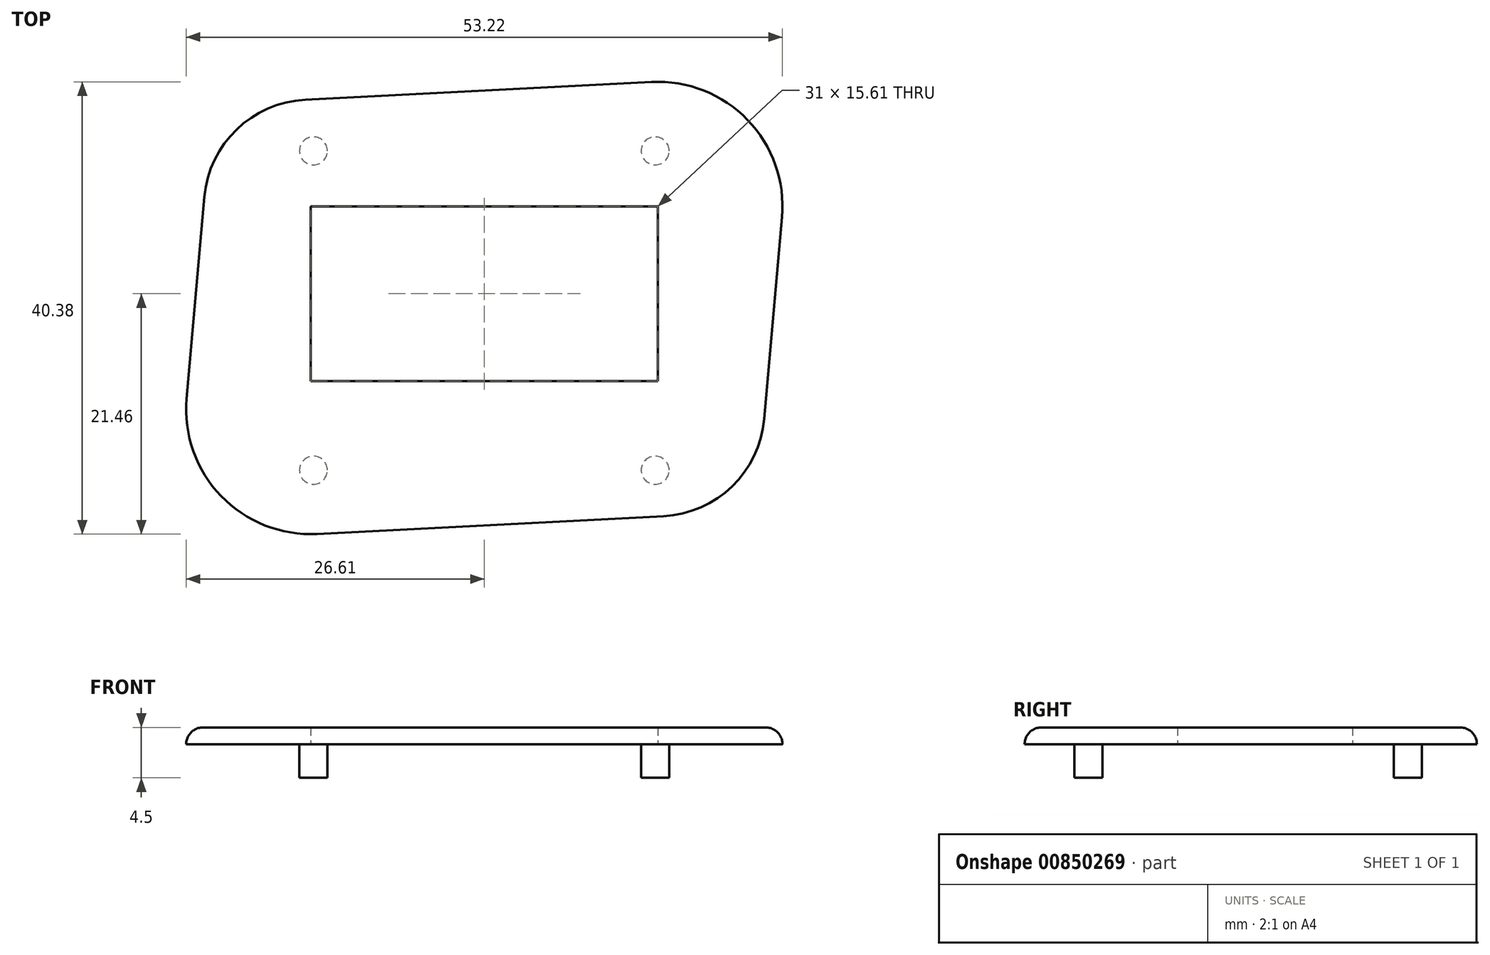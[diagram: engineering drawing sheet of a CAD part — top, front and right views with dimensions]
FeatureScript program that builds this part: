
annotation { "Feature Type Name" : "Feature", "Feature Type Description" : "" }
export const myFeature = defineFeature(function(context is Context, id is Id, definition is map)
    precondition{}
    {
        {
            var Q0;
            Q0=qCreatedBy(makeId("Top.planeOp"),FACE);
            var sketch = newSketch(context, id + "F0", { "sketchPlane" : qUnion([Q0])});
            skLineSegment(sketch, "E0.bottom", {"start": v(17.5, 16.75) * mm, "end": v(-17.5, 16.75) * mm});
            skLineSegment(sketch, "E0.top", {"start": v(17.5, -16.75) * mm, "end": v(-17.5, -16.75) * mm});
            skLineSegment(sketch, "E0.left", {"start": v(17.5, 16.75) * mm, "end": v(17.5, -16.75) * mm});
            skLineSegment(sketch, "E0.right", {"start": v(-17.5, 16.75) * mm, "end": v(-17.5, -16.75) * mm});
            skPoint(sketch, "E0.middle", {"position": v(0, 0) * mm});
            skLineSegment(sketch, "E1.bottom", {"start": v(17.5, 11.3) * mm, "end": v(-17.5, 11.3) * mm});
            skLineSegment(sketch, "E1.top", {"start": v(17.5, -11.3) * mm, "end": v(-17.5, -11.3) * mm});
            skLineSegment(sketch, "E1.left", {"start": v(17.5, 11.3) * mm, "end": v(17.5, -11.3) * mm});
            skLineSegment(sketch, "E1.right", {"start": v(-17.5, 11.3) * mm, "end": v(-17.5, -11.3) * mm});
            skCircle(sketch, "E2", {"center": v(-15.25, 14.25) * mm, "radius": 1.25 * mm});
            skLineSegment(sketch, "E3.bottom", {"start": v(15.25, 14.25) * mm, "end": v(-15.25, 14.25) * mm, "construction": true});
            skLineSegment(sketch, "E3.top", {"start": v(15.25, -14.25) * mm, "end": v(-15.25, -14.25) * mm, "construction": true});
            skLineSegment(sketch, "E3.left", {"start": v(15.25, 14.25) * mm, "end": v(15.25, -14.25) * mm, "construction": true});
            skLineSegment(sketch, "E3.right", {"start": v(-15.25, 14.25) * mm, "end": v(-15.25, -14.25) * mm, "construction": true});
            skCircle(sketch, "E4", {"center": v(15.25, 14.25) * mm, "radius": 1.25 * mm});
            skCircle(sketch, "E5", {"center": v(-15.25, -14.25) * mm, "radius": 1.25 * mm});
            skCircle(sketch, "E6", {"center": v(15.25, -14.25) * mm, "radius": 1.25 * mm});
            skLineSegment(sketch, "E7.bottom", {"start": v(-17.5, 16.75) * mm, "end": v(-19, 16.75) * mm});
            skLineSegment(sketch, "E7.top", {"start": v(-17.5, -16.75) * mm, "end": v(-19, -16.75) * mm});
            skLineSegment(sketch, "E7.right", {"start": v(-19, 16.75) * mm, "end": v(-19, -16.75) * mm});
            skLineSegment(sketch, "E8.bottom", {"start": v(17.5, -16.75) * mm, "end": v(19, -16.75) * mm});
            skLineSegment(sketch, "E8.top", {"start": v(17.5, 16.75) * mm, "end": v(19, 16.75) * mm});
            skLineSegment(sketch, "E8.left", {"start": v(17.5, -16.75) * mm, "end": v(17.5, 16.75) * mm});
            skLineSegment(sketch, "E8.right", {"start": v(19, -16.75) * mm, "end": v(19, 16.75) * mm});
            skSolve(sketch);
        }
        {
            var Q0;
            {var subQ3=sQuery(id+"F0.wireOp",EDGE,"E7.bottom");Q0=makeQuery(id+"F0.imprint","IMPRINT",FACE,{"disambiguationData":[TD([[makeQuery(id+"F0.imprint","IMPRINT",EDGE,{"derivedFrom":subQ3}),1.0]])]});}
            var Q1;
            {var subQ1=sQuery(id+"F0.wireOp",EDGE,"E0.bottom");Q1=makeQuery(id+"F0.imprint","IMPRINT",FACE,{"disambiguationData":[TD([[makeQuery(id+"F0.imprint","IMPRINT",EDGE,{"derivedFrom":subQ1}),1.0]])]});}
            var Q2;
            {var subQ3=sQuery(id+"F0.wireOp",EDGE,"E8.bottom");Q2=makeQuery(id+"F0.imprint","IMPRINT",FACE,{"disambiguationData":[TD([[makeQuery(id+"F0.imprint","IMPRINT",EDGE,{"derivedFrom":subQ3}),1.0]])]});}
            var Q3;
            {var subQ1=sQuery(id+"F0.wireOp",EDGE,"E0.top");Q3=makeQuery(id+"F0.imprint","IMPRINT",FACE,{"disambiguationData":[TD([[makeQuery(id+"F0.imprint","IMPRINT",EDGE,{"derivedFrom":subQ1}),-1.0]])]});}
            extrude(context, id + "F1", {"entities" : qUnion([Q0, Q1, Q2, Q3]), "depth" : 1.5 * mm, "offsetDistance" : 25.4 * mm});
        }
        {
            var Q0;
            Q0=qCreatedBy(makeId("Top.planeOp"),FACE);
            var sketch = newSketch(context, id + "F2", { "sketchPlane" : qUnion([Q0])});
            skLineSegment(sketch, "E9.bottom", {"start": v(-15.5, -6.3) * mm, "end": v(15.5, -6.3) * mm});
            skLineSegment(sketch, "E9.top", {"start": v(-15.5, 9.3) * mm, "end": v(15.5, 9.3) * mm});
            skLineSegment(sketch, "E9.left", {"start": v(-15.5, -6.3) * mm, "end": v(-15.5, 9.3) * mm});
            skLineSegment(sketch, "E9.right", {"start": v(15.5, -6.3) * mm, "end": v(15.5, 9.3) * mm});
            skLineSegment(sketch, "E10.0", {"start": v(-17.5, 11.3) * mm, "end": v(-17.5, -11.3) * mm});
            skLineSegment(sketch, "E10.1", {"start": v(17.5, 11.3) * mm, "end": v(-17.5, 11.3) * mm});
            skLineSegment(sketch, "E10.2", {"start": v(17.5, -11.3) * mm, "end": v(17.5, 11.3) * mm});
            skLineSegment(sketch, "E10.3", {"start": v(17.5, -11.3) * mm, "end": v(-17.5, -11.3) * mm});
            skSolve(sketch);
        }
        {
            var Q0;
            Q0=makeQuery(id+"F2.imprint","IMPRINT",FACE,{"disambiguationData":[TD([[makeQuery(id+"F2.imprint","IMPRINT",EDGE,{"derivedFrom":sQuery(id+"F2.wireOp",EDGE,"E9.bottom")}),-1.0]])]});
            var Q1;
            {var subQ0=sQuery(id+"F0.wireOp",EDGE,"E8.right");var subQ1=sQuery(id+"F0.wireOp",EDGE,"E8.top");var subQ2=sQuery(id+"F0.wireOp",EDGE,"E8.bottom");var subQ3=sQuery(id+"F0.wireOp",EDGE,"E7.right");var subQ4=sQuery(id+"F0.wireOp",EDGE,"E7.top");var subQ5=sQuery(id+"F0.wireOp",EDGE,"E7.bottom");var subQ6=sQuery(id+"F0.wireOp",EDGE,"E0.top");var subQ7=sQuery(id+"F0.wireOp",EDGE,"E0.bottom");Q1=makeQuery(id+"F8.boolean.opBoolean","MERGE",FACE,{"derivedFrom":[makeQuery(id+"F5.boolean.opBoolean","MERGE",FACE,{"derivedFrom":[makeQuery(id+"F1.opExtrude","CAP_FACE",FACE,{"disambiguationData":[OSD([subQ7,subQ6,sQuery(id+"F0.wireOp",EDGE,"E1.bottom"),sQuery(id+"F0.wireOp",EDGE,"E1.top"),sQuery(id+"F0.wireOp",EDGE,"E2"),sQuery(id+"F0.wireOp",EDGE,"E4"),sQuery(id+"F0.wireOp",EDGE,"E5"),sQuery(id+"F0.wireOp",EDGE,"E6"),subQ5,subQ4,sQuery(id+"F0.wireOp",EDGE,"E0.right"),subQ3,subQ2,subQ1,sQuery(id+"F0.wireOp",EDGE,"E8.left"),subQ0])],"isStart":false}),makeQuery(id+"F5.opExtrude","CAP_FACE",FACE,{"disambiguationData":[OSD([sQuery(id+"F4.wireOp",EDGE,"E11.0")])],"isStart":true}),makeQuery(id+"F5.opExtrude","CAP_FACE",FACE,{"disambiguationData":[OSD([sQuery(id+"F4.wireOp",EDGE,"E11.1")])],"isStart":true}),makeQuery(id+"F5.opExtrude","CAP_FACE",FACE,{"disambiguationData":[OSD([sQuery(id+"F4.wireOp",EDGE,"E11.2")])],"isStart":true}),makeQuery(id+"F5.opExtrude","CAP_FACE",FACE,{"disambiguationData":[OSD([sQuery(id+"F4.wireOp",EDGE,"E11.3")])],"isStart":true})]}),makeQuery(id+"F8.opExtrude","CAP_FACE",FACE,{"disambiguationData":[OSD([subQ7,subQ6,subQ5,subQ4,subQ3,subQ2,subQ1,subQ0,sQuery(id+"F6.wireOp",EDGE,"E12"),sQuery(id+"F6.wireOp",EDGE,"E13"),sQuery(id+"F6.wireOp",EDGE,"E14"),sQuery(id+"F6.wireOp",EDGE,"E15"),sQuery(id+"F6.wireOp",EDGE,"E16"),sQuery(id+"F6.wireOp",EDGE,"E17"),sQuery(id+"F6.wireOp",EDGE,"E18"),sQuery(id+"F6.wireOp",EDGE,"E19")])],"isStart":true})]});}
            extrude(context, id + "F3", {"entities" : qUnion([Q0]), "operationType" : NewBodyOperationType.ADD, "endBound" : BoundingType.UP_TO_SURFACE, "depth" : 25.4 * mm, "endBoundEntityFace" : qUnion([Q1]), "offsetDistance" : 25.4 * mm});
        }
        {
            var Q0;
            Q0=makeQuery(id+"F1.opExtrude","CAP_FACE",FACE,{"disambiguationData":[OSD([sQuery(id+"F0.wireOp",EDGE,"E0.bottom"),sQuery(id+"F0.wireOp",EDGE,"E0.top"),sQuery(id+"F0.wireOp",EDGE,"E1.bottom"),sQuery(id+"F0.wireOp",EDGE,"E1.top"),sQuery(id+"F0.wireOp",EDGE,"E2"),sQuery(id+"F0.wireOp",EDGE,"E4"),sQuery(id+"F0.wireOp",EDGE,"E5"),sQuery(id+"F0.wireOp",EDGE,"E6"),sQuery(id+"F0.wireOp",EDGE,"E7.bottom"),sQuery(id+"F0.wireOp",EDGE,"E7.top"),sQuery(id+"F0.wireOp",EDGE,"E0.right"),sQuery(id+"F0.wireOp",EDGE,"E7.right"),sQuery(id+"F0.wireOp",EDGE,"E8.bottom"),sQuery(id+"F0.wireOp",EDGE,"E8.top"),sQuery(id+"F0.wireOp",EDGE,"E8.left"),sQuery(id+"F0.wireOp",EDGE,"E8.right")])],"isStart":false});
            var sketch = newSketch(context, id + "F4", { "sketchPlane" : qUnion([Q0])});
            skCircle(sketch, "E11.0", {"center": v(-15.25, 14.25) * mm, "radius": 1.25 * mm});
            skCircle(sketch, "E11.1", {"center": v(15.25, 14.25) * mm, "radius": 1.25 * mm});
            skCircle(sketch, "E11.2", {"center": v(15.25, -14.25) * mm, "radius": 1.25 * mm});
            skCircle(sketch, "E11.3", {"center": v(-15.25, -14.25) * mm, "radius": 1.25 * mm});
            skSolve(sketch);
        }
        {
            var Q0;
            Q0 = qSketchRegion(id + "F4", true);
            extrude(context, id + "F5", {"entities" : qUnion([Q0]), "operationType" : NewBodyOperationType.ADD, "oppositeDirection" : true, "depth" : 4.5 * mm, "offsetDistance" : 25.4 * mm});
        }
        {
            var Q0;
            Q0=makeQuery(id+"F5.boolean.opBoolean","MERGE",FACE,{"derivedFrom":[makeQuery(id+"F1.opExtrude","CAP_FACE",FACE,{"disambiguationData":[OSD([sQuery(id+"F0.wireOp",EDGE,"E0.bottom"),sQuery(id+"F0.wireOp",EDGE,"E0.top"),sQuery(id+"F0.wireOp",EDGE,"E1.bottom"),sQuery(id+"F0.wireOp",EDGE,"E1.top"),sQuery(id+"F0.wireOp",EDGE,"E2"),sQuery(id+"F0.wireOp",EDGE,"E4"),sQuery(id+"F0.wireOp",EDGE,"E5"),sQuery(id+"F0.wireOp",EDGE,"E6"),sQuery(id+"F0.wireOp",EDGE,"E7.bottom"),sQuery(id+"F0.wireOp",EDGE,"E7.top"),sQuery(id+"F0.wireOp",EDGE,"E0.right"),sQuery(id+"F0.wireOp",EDGE,"E7.right"),sQuery(id+"F0.wireOp",EDGE,"E8.bottom"),sQuery(id+"F0.wireOp",EDGE,"E8.top"),sQuery(id+"F0.wireOp",EDGE,"E8.left"),sQuery(id+"F0.wireOp",EDGE,"E8.right")])],"isStart":false}),makeQuery(id+"F5.opExtrude","CAP_FACE",FACE,{"disambiguationData":[OSD([sQuery(id+"F4.wireOp",EDGE,"E11.0")])],"isStart":true}),makeQuery(id+"F5.opExtrude","CAP_FACE",FACE,{"disambiguationData":[OSD([sQuery(id+"F4.wireOp",EDGE,"E11.1")])],"isStart":true}),makeQuery(id+"F5.opExtrude","CAP_FACE",FACE,{"disambiguationData":[OSD([sQuery(id+"F4.wireOp",EDGE,"E11.2")])],"isStart":true}),makeQuery(id+"F5.opExtrude","CAP_FACE",FACE,{"disambiguationData":[OSD([sQuery(id+"F4.wireOp",EDGE,"E11.3")])],"isStart":true})]});
            var sketch = newSketch(context, id + "F6", { "sketchPlane" : qUnion([Q0])});
            skCircle(sketch, "E12", {"center": v(-15.5, 9.3) * mm, "radius": 9.53 * mm});
            skCircle(sketch, "E13", {"center": v(15.5, -8.84) * mm, "radius": 9.53 * mm});
            skCircle(sketch, "E14", {"center": v(15.5, 9.3) * mm, "radius": 11.11 * mm});
            skCircle(sketch, "E15", {"center": v(-15.5, -8.84) * mm, "radius": 11.11 * mm});
            skLineSegment(sketch, "E16", {"start": v(-24.99, 10.14) * mm, "end": v(-26.57, -7.87) * mm});
            skLineSegment(sketch, "E17", {"start": v(-14.93, -19.94) * mm, "end": v(15.99, -18.36) * mm});
            skLineSegment(sketch, "E18", {"start": v(-15.99, 18.82) * mm, "end": v(14.93, 20.4) * mm});
            skLineSegment(sketch, "E19", {"start": v(26.57, 8.33) * mm, "end": v(24.99, -9.68) * mm});
            skLineSegment(sketch, "E20", {"start": v(15.5, -6.3) * mm, "end": v(15.5, -8.84) * mm, "construction": true});
            skLineSegment(sketch, "E21", {"start": v(15.5, -8.84) * mm, "end": v(-15.5, -8.84) * mm, "construction": true});
            skLineSegment(sketch, "E22", {"start": v(-15.5, -8.84) * mm, "end": v(-15.5, -6.3) * mm, "construction": true});
            skSolve(sketch);
        }
        {
            var Q0;
            {var subQ0=sQuery(id+"F6.wireOp",EDGE,"E17");var subQ1=sQuery(id+"F6.wireOp",EDGE,"E13");var subQ2=makeQuery(id+"F6.imprint","INTERSECT",VERTEX,{"derivedFrom":[subQ1,subQ0]});Q0=makeQuery(id+"F6.imprint","IMPRINT",FACE,{"disambiguationData":[TD([[makeQuery(id+"F6.imprint","IMPRINT",EDGE,{"disambiguationData":[TD([[subQ2,-1.0]])],"derivedFrom":subQ1}),-1.0]])]});}
            var Q1;
            {var subQ0=sQuery(id+"F6.wireOp",EDGE,"E15");var subQ1=makeQuery(id+"F1.opExtrude","CAP_EDGE",EDGE,{"disambiguationData":[OSD([sQuery(id+"F0.wireOp",EDGE,"E7.right")])],"isStart":false});var subQ2=makeQuery(id+"F6.imprint","INTERSECT",VERTEX,{"disambiguationData":[OD(0.0)],"derivedFrom":[subQ1,subQ0]});Q1=makeQuery(id+"F6.imprint","IMPRINT",FACE,{"disambiguationData":[TD([[makeQuery(id+"F6.imprint","IMPRINT",EDGE,{"disambiguationData":[TD([[subQ2,-1.0]])],"derivedFrom":subQ0}),-1.0]])]});}
            extrude(context, id + "F7", {"entities" : qUnion([Q0, Q1]), "operationType" : NewBodyOperationType.REMOVE, "endBound" : BoundingType.THROUGH_ALL, "oppositeDirection" : true, "depth" : 25.4 * mm, "offsetDistance" : 25.4 * mm});
        }
        {
            var Q0;
            {var subQ3=sQuery(id+"F6.wireOp",EDGE,"E12");var subQ5=makeQuery(id+"F6.imprint","INTERSECT",VERTEX,{"derivedFrom":[subQ3,sQuery(id+"F6.wireOp",EDGE,"E16")]});Q0=makeQuery(id+"F6.imprint","IMPRINT",FACE,{"disambiguationData":[TD([[makeQuery(id+"F6.imprint","IMPRINT",EDGE,{"disambiguationData":[TD([[subQ5,1.0]])],"derivedFrom":subQ3}),1.0]])]});}
            var Q1;
            {var subQ0=sQuery(id+"F6.wireOp",EDGE,"E16");Q1=makeQuery(id+"F6.imprint","IMPRINT",FACE,{"disambiguationData":[TD([[makeQuery(id+"F6.imprint","IMPRINT",EDGE,{"derivedFrom":subQ0}),1.0]])]});}
            var Q2;
            {var subQ3=sQuery(id+"F6.wireOp",EDGE,"E15");var subQ5=makeQuery(id+"F6.imprint","INTERSECT",VERTEX,{"derivedFrom":[subQ3,sQuery(id+"F6.wireOp",EDGE,"E16")]});Q2=makeQuery(id+"F6.imprint","IMPRINT",FACE,{"disambiguationData":[TD([[makeQuery(id+"F6.imprint","IMPRINT",EDGE,{"disambiguationData":[TD([[subQ5,1.0]])],"derivedFrom":subQ3}),1.0]])]});}
            var Q3;
            {var subQ0=sQuery(id+"F6.wireOp",EDGE,"E17");Q3=makeQuery(id+"F6.imprint","IMPRINT",FACE,{"disambiguationData":[TD([[makeQuery(id+"F6.imprint","IMPRINT",EDGE,{"derivedFrom":subQ0}),1.0]])]});}
            var Q4;
            {var subQ0=sQuery(id+"F6.wireOp",EDGE,"E13");var subQ7=makeQuery(id+"F6.imprint","INTERSECT",VERTEX,{"derivedFrom":[subQ0,sQuery(id+"F6.wireOp",EDGE,"E17")]});Q4=makeQuery(id+"F6.imprint","IMPRINT",FACE,{"disambiguationData":[TD([[makeQuery(id+"F6.imprint","IMPRINT",EDGE,{"disambiguationData":[TD([[subQ7,-1.0]])],"derivedFrom":subQ0}),1.0]])]});}
            var Q5;
            {var subQ0=sQuery(id+"F6.wireOp",EDGE,"E19");Q5=makeQuery(id+"F6.imprint","IMPRINT",FACE,{"disambiguationData":[TD([[makeQuery(id+"F6.imprint","IMPRINT",EDGE,{"derivedFrom":subQ0}),-1.0]])]});}
            var Q6;
            {var subQ3=sQuery(id+"F6.wireOp",EDGE,"E14");var subQ5=makeQuery(id+"F6.imprint","INTERSECT",VERTEX,{"derivedFrom":[subQ3,sQuery(id+"F6.wireOp",EDGE,"E19")]});Q6=makeQuery(id+"F6.imprint","IMPRINT",FACE,{"disambiguationData":[TD([[makeQuery(id+"F6.imprint","IMPRINT",EDGE,{"disambiguationData":[TD([[subQ5,1.0]])],"derivedFrom":subQ3}),1.0]])]});}
            var Q7;
            {var subQ0=sQuery(id+"F6.wireOp",EDGE,"E18");Q7=makeQuery(id+"F6.imprint","IMPRINT",FACE,{"disambiguationData":[TD([[makeQuery(id+"F6.imprint","IMPRINT",EDGE,{"derivedFrom":subQ0}),-1.0]])]});}
            var Q8;
            {var subQ0=sQuery(id+"F6.wireOp",EDGE,"E14");var subQ1=sQuery(id+"F6.wireOp",EDGE,"E13");var subQ2=makeQuery(id+"F6.imprint","INTERSECT",VERTEX,{"disambiguationData":[OD(0.0)],"derivedFrom":[subQ1,subQ0]});Q8=makeQuery(id+"F6.imprint","IMPRINT",FACE,{"disambiguationData":[TD([[makeQuery(id+"F6.imprint","IMPRINT",EDGE,{"disambiguationData":[TD([[subQ2,-1.0]])],"derivedFrom":subQ1}),1.0]])]});}
            var Q9;
            {var subQ0=sQuery(id+"F6.wireOp",EDGE,"E15");var subQ1=sQuery(id+"F6.wireOp",EDGE,"E12");var subQ2=makeQuery(id+"F6.imprint","INTERSECT",VERTEX,{"disambiguationData":[OD(0.0)],"derivedFrom":[subQ1,subQ0]});Q9=makeQuery(id+"F6.imprint","IMPRINT",FACE,{"disambiguationData":[TD([[makeQuery(id+"F6.imprint","IMPRINT",EDGE,{"disambiguationData":[TD([[subQ2,-1.0]])],"derivedFrom":subQ1}),1.0]])]});}
            var Q10;
            {var subQ0=sQuery(id+"F6.wireOp",EDGE,"E13");var subQ1=makeQuery(id+"F6.imprint","INTERSECT",VERTEX,{"derivedFrom":[subQ0,sQuery(id+"F6.wireOp",EDGE,"E19")]});Q10=makeQuery(id+"F6.imprint","IMPRINT",FACE,{"disambiguationData":[TD([[makeQuery(id+"F6.imprint","IMPRINT",EDGE,{"disambiguationData":[TD([[subQ1,1.0]])],"derivedFrom":subQ0}),1.0]])]});}
            var Q11;
            {var subQ0=sQuery(id+"F6.wireOp",EDGE,"E15");var subQ1=makeQuery(id+"F6.imprint","INTERSECT",VERTEX,{"derivedFrom":[subQ0,sQuery(id+"F6.wireOp",EDGE,"E17")]});Q11=makeQuery(id+"F6.imprint","IMPRINT",FACE,{"disambiguationData":[TD([[makeQuery(id+"F6.imprint","IMPRINT",EDGE,{"disambiguationData":[TD([[subQ1,1.0]])],"derivedFrom":subQ0}),1.0]])]});}
            extrude(context, id + "F8", {"entities" : qUnion([Q0, Q1, Q2, Q3, Q4, Q5, Q6, Q7, Q8, Q9, Q10, Q11]), "operationType" : NewBodyOperationType.ADD, "oppositeDirection" : true, "depth" : 1.5 * mm, "offsetDistance" : 25.4 * mm});
        }
        {
            var Q0;
            Q0=makeQuery(id+"F8.opExtrude","CAP_EDGE",EDGE,{"disambiguationData":[OSD([sQuery(id+"F6.wireOp",EDGE,"E15")])],"isStart":true});
            fillet(context, id + "F9", {"entities" : qUnion([Q0]), "radius" : 1.5 * mm, "tangentPropagation" : true, "defaultsChanged" : false, "vertexSettings" : [], "allowEdgeOverflow" : false});
        }
    });
